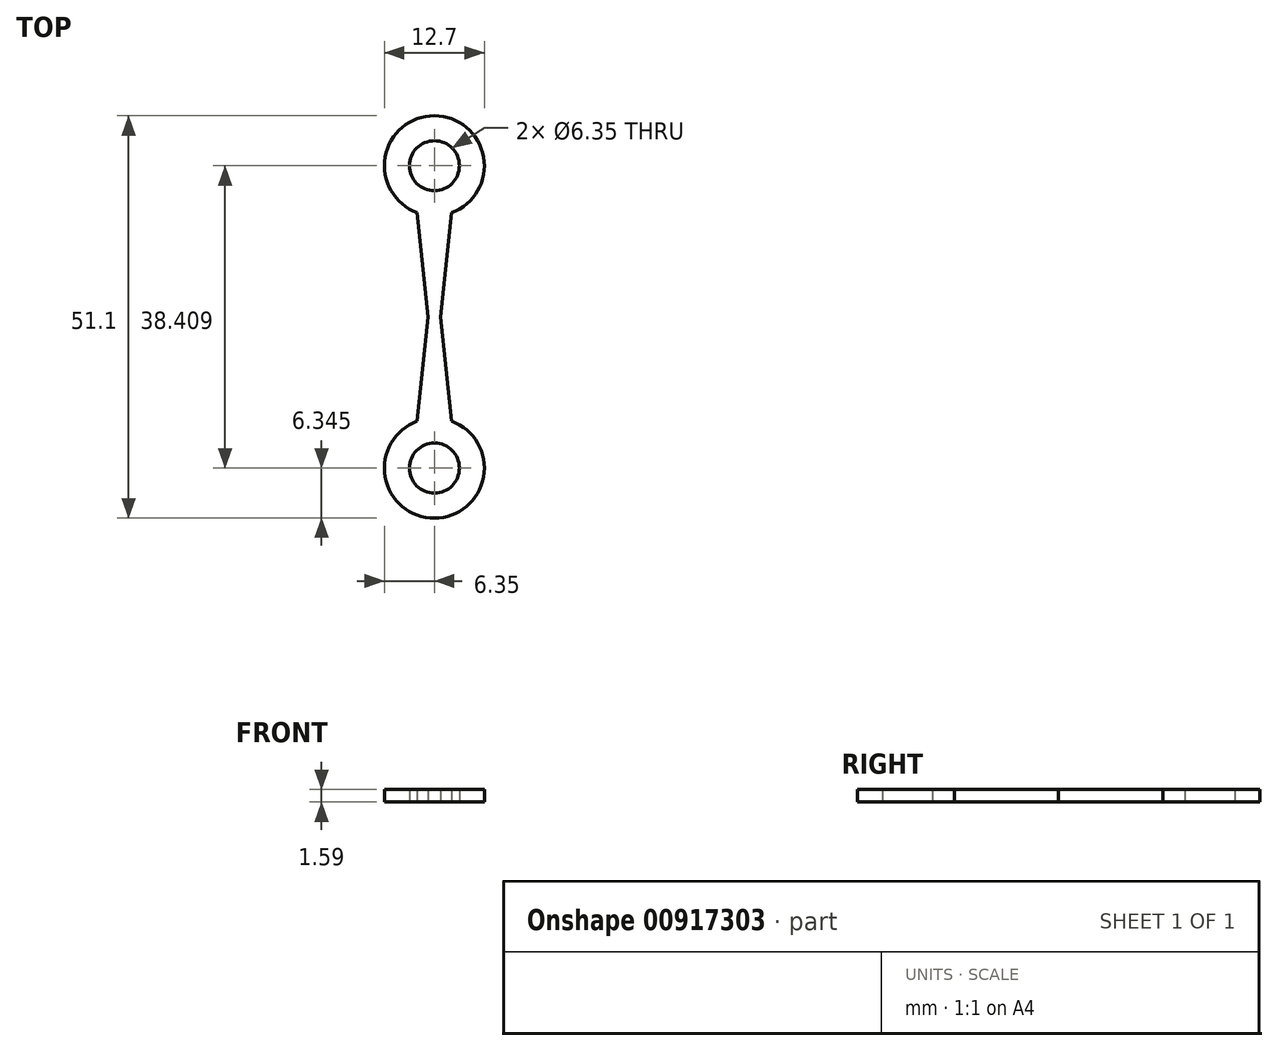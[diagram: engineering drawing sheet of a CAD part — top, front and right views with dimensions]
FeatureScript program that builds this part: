
annotation { "Feature Type Name" : "Feature", "Feature Type Description" : "" }
export const myFeature = defineFeature(function(context is Context, id is Id, definition is map)
    precondition{}
    {
        {
            var Q0;
            Q0=qCreatedBy(makeId("Top.planeOp"),FACE);
            var sketch = newSketch(context, id + "F0", { "sketchPlane" : qUnion([Q0])});
            skArc(sketch, "E0", {"start": v(2.19, 13.24) * mm, "mid": v(0, 25.55) * mm, "end": v(-2.19, 13.24) * mm});
            skCircle(sketch, "E1", {"center": v(0, 19.2) * mm, "radius": 3.18 * mm});
            skLineSegment(sketch, "E2", {"start": v(-0.8, 0) * mm, "end": v(0.8, 0) * mm, "construction": true});
            skLineSegment(sketch, "E3", {"start": v(-0.8, 0) * mm, "end": v(-2.19, 13.24) * mm});
            skLineSegment(sketch, "E4.MirrorCS", {"start": v(0.8, 0) * mm, "end": v(2.19, 13.24) * mm});
            skLineSegment(sketch, "E5.MirrorCS", {"start": v(0.8, 0) * mm, "end": v(2.19, -13.24) * mm});
            skLineSegment(sketch, "E6.MirrorCS", {"start": v(-0.8, 0) * mm, "end": v(-2.19, -13.24) * mm});
            skArc(sketch, "E7.MirrorCS", {"start": v(2.19, -13.24) * mm, "mid": v(0, -25.55) * mm, "end": v(-2.19, -13.24) * mm});
            skCircle(sketch, "E8.MirrorC", {"center": v(0, -19.2) * mm, "radius": 3.18 * mm});
            skSolve(sketch);
        }
        {
            var Q0;
            Q0 = qSketchRegion(id + "F0", true);
            extrude(context, id + "F1", {"entities" : qUnion([Q0]), "depth" : 1.59 * mm, "offsetDistance" : 25.4 * mm});
        }
    });
